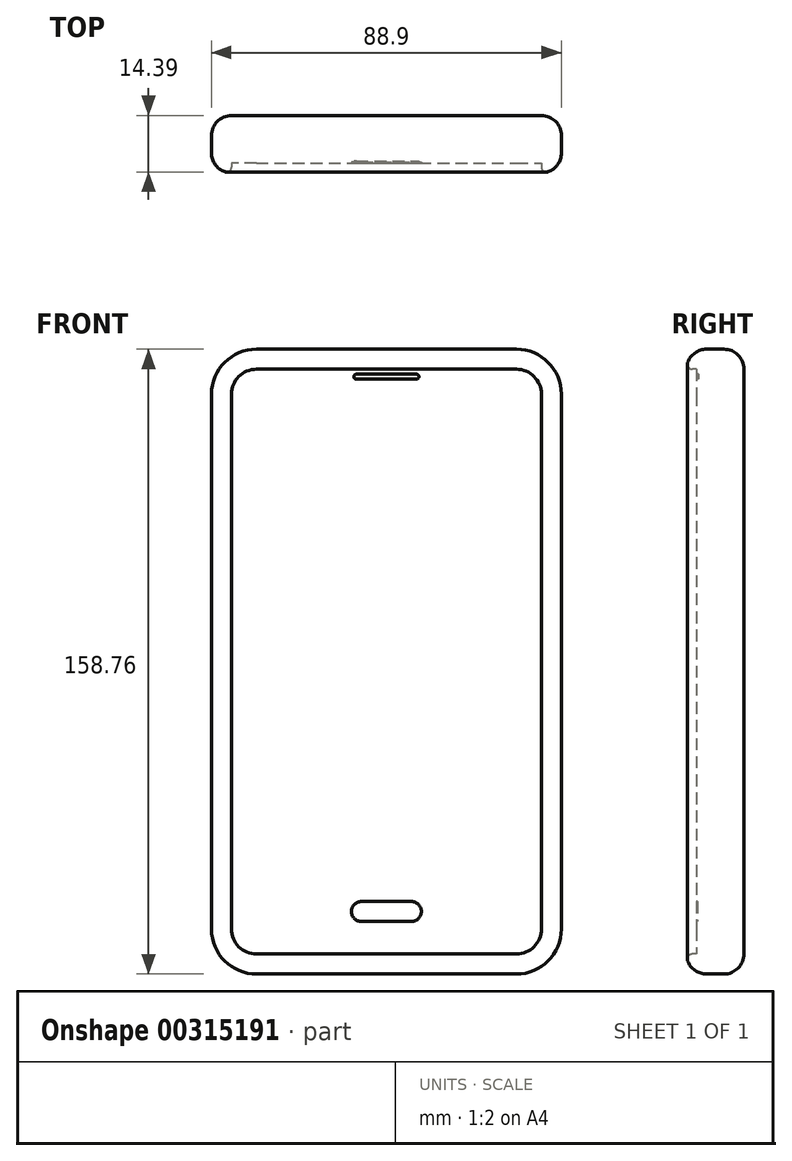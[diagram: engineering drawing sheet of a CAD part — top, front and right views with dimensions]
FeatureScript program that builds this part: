
annotation { "Feature Type Name" : "Feature", "Feature Type Description" : "" }
export const myFeature = defineFeature(function(context is Context, id is Id, definition is map)
    precondition{}
    {
        {
            var Q0;
            Q0=qCreatedBy(makeId("Front.planeOp"),FACE);
            var sketch = newSketch(context, id + "F0", { "sketchPlane" : qUnion([Q0])});
            skLineSegment(sketch, "E0.bottom", {"start": v(-33.02, 79.38) * mm, "end": v(33.02, 79.38) * mm});
            skLineSegment(sketch, "E0.top", {"start": v(-33.02, -79.38) * mm, "end": v(33.02, -79.38) * mm});
            skLineSegment(sketch, "E0.left", {"start": v(-44.45, 67.95) * mm, "end": v(-44.45, -67.95) * mm});
            skLineSegment(sketch, "E0.right", {"start": v(44.45, 67.95) * mm, "end": v(44.45, -67.95) * mm});
            skPoint(sketch, "E0.middle", {"position": v(0, 0) * mm});
            skPoint(sketch, "E1.visualSharp", {"position": v(-44.45, 79.38) * mm});
            skArc(sketch, "E1.filletArc", {"start": v(-33.02, 79.38) * mm, "mid": v(-41.1, 76.03) * mm, "end": v(-44.45, 67.95) * mm});
            skPoint(sketch, "E2.visualSharp", {"position": v(44.45, 79.38) * mm});
            skArc(sketch, "E2.filletArc", {"start": v(44.45, 67.95) * mm, "mid": v(41.1, 76.03) * mm, "end": v(33.02, 79.38) * mm});
            skPoint(sketch, "E3.visualSharp", {"position": v(44.45, -79.38) * mm});
            skArc(sketch, "E3.filletArc", {"start": v(33.02, -79.38) * mm, "mid": v(41.1, -76.03) * mm, "end": v(44.45, -67.95) * mm});
            skPoint(sketch, "E4.visualSharp", {"position": v(-44.45, -79.38) * mm});
            skArc(sketch, "E4.filletArc", {"start": v(-44.45, -67.95) * mm, "mid": v(-41.1, -76.03) * mm, "end": v(-33.02, -79.38) * mm});
            skSolve(sketch);
        }
        {
            var Q0;
            Q0 = qSketchRegion(id + "F0", true);
            extrude(context, id + "F1", {"entities" : qUnion([Q0]), "oppositeDirection" : true, "depth" : 14.6 * mm});
        }
        {
            var Q0;
            Q0=makeQuery(id+"F1.opExtrude","CAP_FACE",FACE,{"disambiguationData":[OSD([sQuery(id+"F0.wireOp",EDGE,"E0.bottom"),sQuery(id+"F0.wireOp",EDGE,"E0.top"),sQuery(id+"F0.wireOp",EDGE,"E0.left"),sQuery(id+"F0.wireOp",EDGE,"E0.right"),sQuery(id+"F0.wireOp",EDGE,"E1.filletArc"),sQuery(id+"F0.wireOp",EDGE,"E2.filletArc"),sQuery(id+"F0.wireOp",EDGE,"E3.filletArc"),sQuery(id+"F0.wireOp",EDGE,"E4.filletArc")])],"isStart":true});
            var sketch = newSketch(context, id + "F2", { "sketchPlane" : qUnion([Q0])});
            skLineSegment(sketch, "E5.0", {"start": v(-39.37, 67.95) * mm, "end": v(-39.37, -67.95) * mm});
            skArc(sketch, "E5.1", {"start": v(-33.02, 74.3) * mm, "mid": v(-37.51, 72.44) * mm, "end": v(-39.37, 67.95) * mm});
            skArc(sketch, "E5.2", {"start": v(-39.37, -67.95) * mm, "mid": v(-37.51, -72.44) * mm, "end": v(-33.02, -74.3) * mm});
            skLineSegment(sketch, "E5.3", {"start": v(33.02, 74.3) * mm, "end": v(-33.02, 74.3) * mm});
            skLineSegment(sketch, "E5.4", {"start": v(-33.02, -74.3) * mm, "end": v(33.02, -74.3) * mm});
            skArc(sketch, "E5.5", {"start": v(33.02, -74.3) * mm, "mid": v(37.51, -72.44) * mm, "end": v(39.37, -67.95) * mm});
            skLineSegment(sketch, "E5.6", {"start": v(39.37, -67.95) * mm, "end": v(39.37, 67.95) * mm});
            skArc(sketch, "E5.7", {"start": v(39.37, 67.95) * mm, "mid": v(37.51, 72.44) * mm, "end": v(33.02, 74.3) * mm});
            skSolve(sketch);
        }
        {
            var Q0;
            Q0 = qSketchRegion(id + "F2", true);
            extrude(context, id + "F3", {"entities" : qUnion([Q0]), "operationType" : NewBodyOperationType.REMOVE, "oppositeDirection" : true, "depth" : 2.54 * mm});
        }
        {
            var Q0;
            Q0=makeQuery(id+"F1.opExtrude","CAP_EDGE",EDGE,{"disambiguationData":[OSD([sQuery(id+"F0.wireOp",EDGE,"E4.filletArc")])],"isStart":true});
            var Q1;
            Q1=makeQuery(id+"F1.opExtrude","CAP_EDGE",EDGE,{"disambiguationData":[OSD([sQuery(id+"F0.wireOp",EDGE,"E0.top")])],"isStart":false});
            fillet(context, id + "F4", {"entities" : qUnion([Q0, Q1]), "radius" : 5.08 * mm, "tangentPropagation" : true, "allowEdgeOverflow" : false});
        }
        {
            var Q0;
            Q0=makeQuery(id+"F4.opFillet","BLEND_EDGE",EDGE,{"blendedFrom":[makeQuery(id+"F1.opExtrude","CAP_EDGE",EDGE,{"disambiguationData":[OSD([sQuery(id+"F0.wireOp",EDGE,"E0.left")])],"isStart":true}),makeQuery(id+"F3.boolean.opBoolean","COPY",FACE,{"derivedFrom":makeQuery(id+"F3.opExtrude","SWEPT_FACE",FACE,{"disambiguationData":[OSD([sQuery(id+"F2.wireOp",EDGE,"E5.0")])]})})],"blendedInto":[makeQuery(id+"F3.boolean.opBoolean","COPY",FACE,{"derivedFrom":makeQuery(id+"F3.opExtrude","SWEPT_FACE",FACE,{"disambiguationData":[OSD([sQuery(id+"F2.wireOp",EDGE,"E5.0")])]})})]});
            fillet(context, id + "F5", {"entities" : qUnion([Q0]), "radius" : 1.27 * mm, "tangentPropagation" : true, "allowEdgeOverflow" : false});
        }
        {
            var Q0;
            Q0=makeQuery(id+"F3.boolean.opBoolean","COPY",FACE,{"derivedFrom":makeQuery(id+"F3.opExtrude","CAP_FACE",FACE,{"disambiguationData":[OSD([sQuery(id+"F2.wireOp",EDGE,"E5.0"),sQuery(id+"F2.wireOp",EDGE,"E5.1"),sQuery(id+"F2.wireOp",EDGE,"E5.2"),sQuery(id+"F2.wireOp",EDGE,"E5.3"),sQuery(id+"F2.wireOp",EDGE,"E5.4"),sQuery(id+"F2.wireOp",EDGE,"E5.5"),sQuery(id+"F2.wireOp",EDGE,"E5.6"),sQuery(id+"F2.wireOp",EDGE,"E5.7")])],"isStart":false})});
            var sketch = newSketch(context, id + "F6", { "sketchPlane" : qUnion([Q0])});
            skLineSegment(sketch, "E6", {"start": v(0, 0) * mm, "end": v(0, -74.3) * mm, "construction": true});
            skLineSegment(sketch, "E7", {"start": v(-6.35, -63.5) * mm, "end": v(6.35, -63.5) * mm, "construction": true});
            skArc(sketch, "E8.0.startCap", {"start": v(-6.35, -66.04) * mm, "mid": v(-8.9, -63.5) * mm, "end": v(-6.35, -60.96) * mm});
            skArc(sketch, "E8.0.endCap", {"start": v(6.35, -60.96) * mm, "mid": v(8.89, -63.5) * mm, "end": v(6.35, -66.04) * mm});
            skLineSegment(sketch, "E8.0.left", {"start": v(-6.35, -60.96) * mm, "end": v(6.35, -60.96) * mm});
            skLineSegment(sketch, "E8.0.right", {"start": v(-6.35, -66.04) * mm, "end": v(6.35, -66.04) * mm});
            skArc(sketch, "E9.0", {"start": v(6.35, -60.83) * mm, "mid": v(9.02, -63.5) * mm, "end": v(6.35, -66.16) * mm});
            skArc(sketch, "E10.0", {"start": v(33.02, -80.64) * mm, "mid": v(42, -76.93) * mm, "end": v(45.72, -67.95) * mm});
            skLineSegment(sketch, "E10.1", {"start": v(-33.02, -80.64) * mm, "end": v(33.02, -80.64) * mm});
            skLineSegment(sketch, "E10.2", {"start": v(45.72, -67.95) * mm, "end": v(45.72, 67.95) * mm});
            skArc(sketch, "E10.3", {"start": v(-45.72, -67.95) * mm, "mid": v(-42, -76.93) * mm, "end": v(-33.02, -80.64) * mm});
            skArc(sketch, "E10.4", {"start": v(45.72, 67.95) * mm, "mid": v(42, 76.93) * mm, "end": v(33.02, 80.65) * mm});
            skLineSegment(sketch, "E10.5", {"start": v(33.02, 80.64) * mm, "end": v(-33.02, 80.64) * mm});
            skArc(sketch, "E10.6", {"start": v(-33.02, 80.64) * mm, "mid": v(-42, 76.93) * mm, "end": v(-45.72, 67.95) * mm});
            skLineSegment(sketch, "E10.7", {"start": v(-45.72, 67.95) * mm, "end": v(-45.72, -67.95) * mm});
            skLineSegment(sketch, "E11.0", {"start": v(-6.35, -60.83) * mm, "end": v(6.35, -60.83) * mm});
            skArc(sketch, "E11.1", {"start": v(-6.35, -66.16) * mm, "mid": v(-9.02, -63.5) * mm, "end": v(-6.35, -60.83) * mm});
            skLineSegment(sketch, "E11.2", {"start": v(-6.35, -66.16) * mm, "end": v(6.35, -66.16) * mm});
            skSolve(sketch);
        }
        {
            var Q0;
            Q0=makeQuery(id+"F6.imprint","IMPRINT",FACE,{"disambiguationData":[TD([[makeQuery(id+"F6.imprint","IMPRINT",EDGE,{"derivedFrom":sQuery(id+"F6.wireOp",EDGE,"E8.0.startCap")}),1.0]])]});
            extrude(context, id + "F7", {"entities" : qUnion([Q0]), "operationType" : NewBodyOperationType.REMOVE, "oppositeDirection" : true, "depth" : 0.25 * mm});
        }
        {
            var Q0;
            Q0=makeQuery(id+"F3.boolean.opBoolean","COPY",FACE,{"derivedFrom":makeQuery(id+"F3.opExtrude","CAP_FACE",FACE,{"disambiguationData":[OSD([sQuery(id+"F2.wireOp",EDGE,"E5.0"),sQuery(id+"F2.wireOp",EDGE,"E5.1"),sQuery(id+"F2.wireOp",EDGE,"E5.2"),sQuery(id+"F2.wireOp",EDGE,"E5.3"),sQuery(id+"F2.wireOp",EDGE,"E5.4"),sQuery(id+"F2.wireOp",EDGE,"E5.5"),sQuery(id+"F2.wireOp",EDGE,"E5.6"),sQuery(id+"F2.wireOp",EDGE,"E5.7")])],"isStart":false})});
            var sketch = newSketch(context, id + "F8", { "sketchPlane" : qUnion([Q0])});
            skLineSegment(sketch, "E12", {"start": v(-7.62, 72.39) * mm, "end": v(7.62, 72.39) * mm, "construction": true});
            skLineSegment(sketch, "E13", {"start": v(0, 0) * mm, "end": v(0, 74.3) * mm, "construction": true});
            skArc(sketch, "E14.0.startCap", {"start": v(-7.62, 71.75) * mm, "mid": v(-8.25, 72.39) * mm, "end": v(-7.62, 73.02) * mm});
            skArc(sketch, "E14.0.endCap", {"start": v(7.62, 73.02) * mm, "mid": v(8.26, 72.39) * mm, "end": v(7.62, 71.75) * mm});
            skLineSegment(sketch, "E14.0.left", {"start": v(-7.62, 73.02) * mm, "end": v(7.62, 73.02) * mm});
            skLineSegment(sketch, "E14.0.right", {"start": v(-7.62, 71.75) * mm, "end": v(7.62, 71.75) * mm});
            skSolve(sketch);
        }
        {
            var Q0;
            Q0 = qSketchRegion(id + "F8", true);
            extrude(context, id + "F9", {"entities" : qUnion([Q0]), "operationType" : NewBodyOperationType.REMOVE, "oppositeDirection" : true, "depth" : 0.5 * mm});
        }
    });
